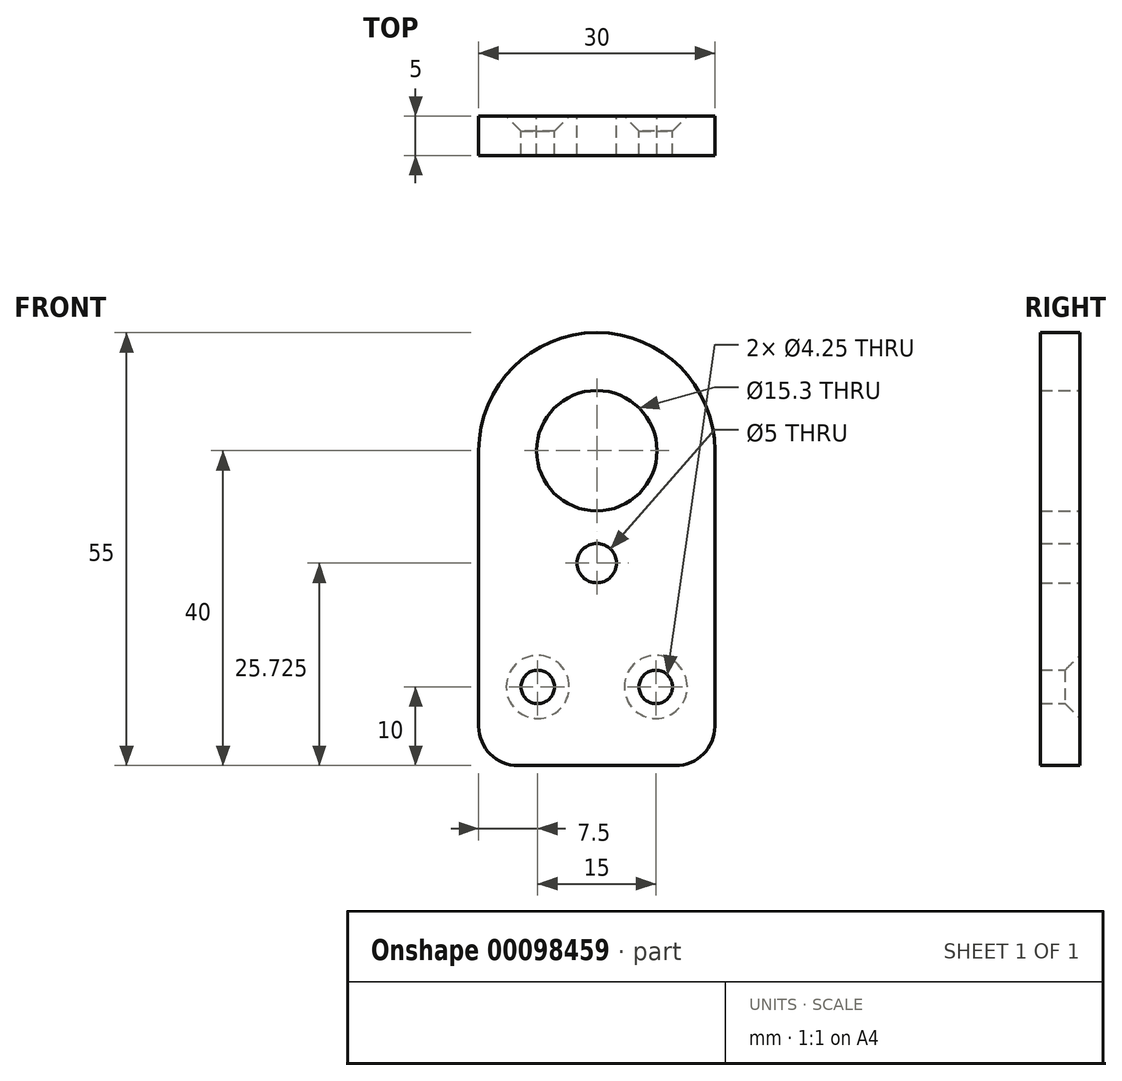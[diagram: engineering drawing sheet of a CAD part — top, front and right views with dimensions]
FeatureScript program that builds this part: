
annotation { "Feature Type Name" : "Feature", "Feature Type Description" : "" }
export const myFeature = defineFeature(function(context is Context, id is Id, definition is map)
    precondition{}
    {
        {
            var Q0;
            Q0=qCreatedBy(makeId("Front.planeOp"),FACE);
            var sketch = newSketch(context, id + "F0", { "sketchPlane" : qUnion([Q0])});
            skLineSegment(sketch, "E0", {"start": v(0, 0) * mm, "end": v(15, 0) * mm});
            skLineSegment(sketch, "E1", {"start": v(15, 0) * mm, "end": v(15, 40) * mm});
            skLineSegment(sketch, "E2.MirrorCS", {"start": v(-15, 0) * mm, "end": v(-15, 40) * mm});
            skLineSegment(sketch, "E3.MirrorCS", {"start": v(0, 0) * mm, "end": v(-15, 0) * mm});
            skArc(sketch, "E4", {"start": v(15, 40) * mm, "mid": v(0, 55) * mm, "end": v(-15, 40) * mm});
            skCircle(sketch, "E5", {"center": v(0, 40) * mm, "radius": 7.65 * mm});
            skLineSegment(sketch, "E6", {"start": v(-15, 10) * mm, "end": v(15, 10) * mm, "construction": true});
            skCircle(sketch, "E7", {"center": v(7.5, 10) * mm, "radius": 4 * mm, "construction": true});
            skPoint(sketch, "E7.centerSnap0", {"position": v(7.5, 0) * mm});
            skCircle(sketch, "E8.MirrorC", {"center": v(-7.5, 10) * mm, "radius": 4 * mm, "construction": true});
            skCircle(sketch, "E9", {"center": v(0, 40) * mm, "radius": 9 * mm, "construction": true});
            skCircle(sketch, "E10", {"center": v(0, 25.73) * mm, "radius": 2.5 * mm});
            skSolve(sketch);
        }
        {
            var Q0;
            Q0 = qSketchRegion(id + "F0", true);
            extrude(context, id + "F1", {"entities" : qUnion([Q0]), "depth" : 5 * mm});
        }
        {
            var Q0;
            Q0=sQuery(id+"F0.wireOp",VERTEX,"E8.MirrorC.center");
            var Q1;
            Q1=sQuery(id+"F0.wireOp",VERTEX,"E7.center");
            var Q2;
            Q2=makeQuery(id+"F1.opExtrude","SWEPT_BODY",BODY,{"disambiguationData":[OSD([sQuery(id+"F0.wireOp",EDGE,"E0"),sQuery(id+"F0.wireOp",EDGE,"E1"),sQuery(id+"F0.wireOp",EDGE,"E2.MirrorCS"),sQuery(id+"F0.wireOp",EDGE,"E3.MirrorCS"),sQuery(id+"F0.wireOp",EDGE,"E4"),sQuery(id+"F0.wireOp",EDGE,"E5")])]});
            hole(context, id + "F2", {"style" : HoleStyle.C_SINK, "endStyle" : HoleEndStyle.THROUGH, "oppositeDirection" : true, "holeDiameter" : 4.25 * mm, "cSinkDiameter" : 8 * mm, "cSinkAngle" : 90 * degree, "locations" : qUnion([Q0, Q1]), "scope" : qUnion([Q2]), "isTappedThrough" : true});
        }
        {
            var Q0;
            Q0=makeQuery(id+"F1.opExtrude","SWEPT_EDGE",EDGE,{"disambiguationData":[OSD([sQuery(id+"F0.wireOp",EDGE,"E2.MirrorCS"),sQuery(id+"F0.wireOp",EDGE,"E3.MirrorCS")])]});
            var Q1;
            Q1=makeQuery(id+"F1.opExtrude","SWEPT_EDGE",EDGE,{"disambiguationData":[OSD([sQuery(id+"F0.wireOp",EDGE,"E0"),sQuery(id+"F0.wireOp",EDGE,"E1")])]});
            fillet(context, id + "F3", {"entities" : qUnion([Q0, Q1]), "radius" : 5 * mm, "tangentPropagation" : true, "allowEdgeOverflow" : false});
        }
    });
